# Revit family: ROTHOB_Rothoblaas_Tape_WindowBand
name_source: partatom
category: Structural Connections
units: mm (PartAtom-declared; Revit-internal decimal feet)

## family parameters
Cut with Voids When Loaded = No
Enable cutting in views = Yes
Host = Face
Material for Model Behavior = Other
OmniClass Number = 23.13.23.17
OmniClass Title = General Purpose Tape
Shared = No

## types (1)
- WINDOW BAND
    Airtightness = α ≤ 1.0 m3/(h·m·(dPa)2/3)
    ApplicationTemperature = +5/+30 °C
    BIMObjectName = ROTHOB_Rothoblaas_Tape_WindowBand
    Category = Pr_35_90_87_63 - Polyurethane (PU) foam strips
    Color = Black
    Default Elevation = 1.22 m
    Description = Self-expanding sealing tape for doors/windows
    DurationUnit = Years
    EMCODECode = 19323/03.03.10
    EMICODE = EC1 plus
    Esporta tipo in formato IFC con nome = IfcBuildingElementProxyType
    ExposureClass = MF1 (BG1/BGR)
    FrenchVOC_Classification = A+
    IfcExportAs = IfcBuildingElementProxyType
    IfcExportType = USERDEFINED
    ManufacturerName = ROTHO BLAAS SRL
    ManufacturerURL = www.rothoblaas.com
    Material = Elastic polyurethane foam with additives
    ModelDisclaimer = The latest version of the data sheets can be found on our website
    Name = Tape
    ObjectMaterial = ROTHOB_Rothoblaas_Polyurethane
    OmniClassCode = 23.13 23.17
    OmniClassTitle = General Purpose Tape
    OmniClassVersion = 2012-05-16
    ProductInformation = https://www.rothoblaas.com
    ReactionFire = class B1
    ResistanceTemperature = -20/+80 °C
    Shape = Bidimensional
    SoundproofingJoints = 10 mm: ≥ 59 (-2; -3) db
    ThermalConductivity = ≤ 0,050 W/(m·K)
    Tightness_HeavyRain = ≥ 600 Pa
    Tipo IFC predefinito = USERDEFINED
    UniClass2015Code = Pr_35_90_87_63
    UniClass2015Title = Polyurethane (PU) foam strips
    UniClass2015Version = Products v1.33
    Version = 1
